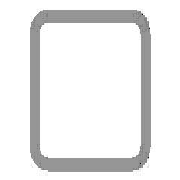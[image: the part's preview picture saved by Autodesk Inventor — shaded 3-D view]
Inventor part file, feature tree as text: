
AUTODESK INVENTOR PART (.ipt)
format: ipt  version: 2022 (Build 260153000, 153)  size: 156,160 bytes
history: native  units: mm (DEFAULTED — no unit token found)
features: other x4, plane x3, sketch x3, split x2, extrude x1
ambient origin geometry x8: Origin, YZ Plane, XZ Plane, XY Plane, X Axis, Y Axis, Z Axis, Center Point
bodies: Solid1 (feature_tree)
feature tree (13):
  parser-record x1  (decoder bookkeeping rows leaked as tree rows — omitted from the tree; the rows remain in map.json)
  other  "Driven Length"
  other  "Plano inicial"
  other  "Plano final"
  extrude  "Cuerpo"  TaperAngle=0.0deg  [1 undecoded]
  plane  "Plano de trabajo4"
  split  "Dividir1"
  plane  "Plano de trabajo5"
  split  "Dividir2"
  sketch  "Boceto"  dims[d10=40.0mm d11=40.0mm d12=5.0mm d13=-5.182521mm d14=217.68067mm d15=20.0mm d16=20.0mm d17=90.0deg d18=222.86319mm]
  sketch  "Sketch3"  dims[d3=222.86319mm d4=0.0mm]
  plane  "Work Plane3"
  sketch  "Sketch4"  dims[d7=7.5mm]
note: 1 required parameter value undecoded (feature->parameter linkage not recoverable at this tier; creation-order binding heuristic only, values carry confidence <= 0.55)
